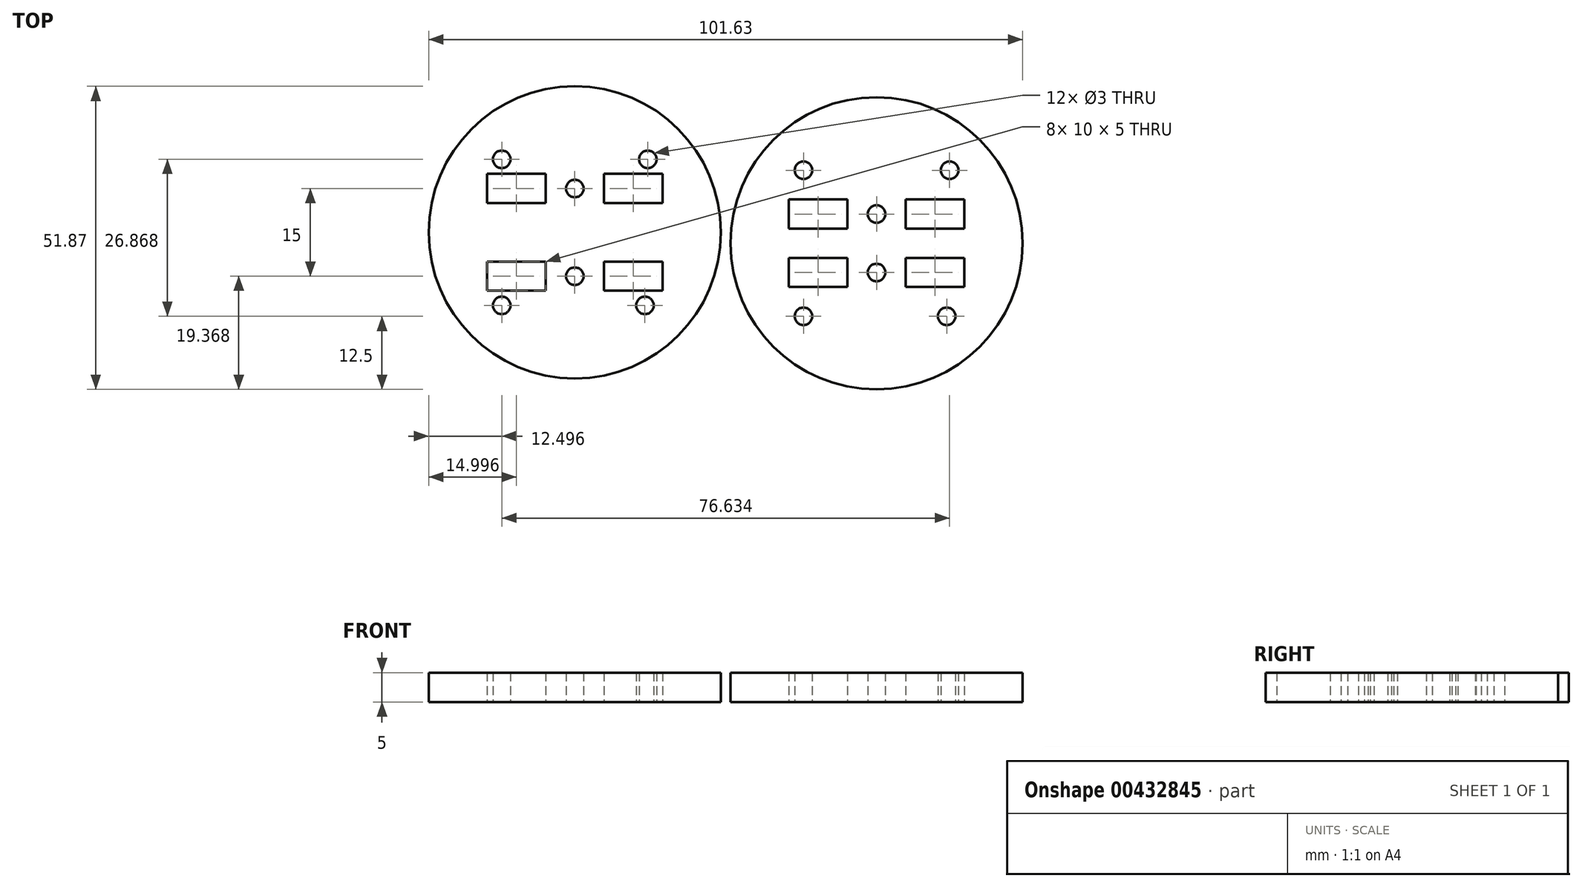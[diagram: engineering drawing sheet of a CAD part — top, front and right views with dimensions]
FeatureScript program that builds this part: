
annotation { "Feature Type Name" : "Feature", "Feature Type Description" : "" }
export const myFeature = defineFeature(function(context is Context, id is Id, definition is map)
    precondition{}
    {
        {
            var Q0;
            Q0=qCreatedBy(makeId("Top.planeOp"),FACE);
            var sketch = newSketch(context, id + "F0", { "sketchPlane" : qUnion([Q0])});
            skCircle(sketch, "E0", {"center": v(0, 0) * mm, "radius": 25 * mm});
            skCircle(sketch, "E1", {"center": v(0, 5) * mm, "radius": 1.5 * mm});
            skCircle(sketch, "E2", {"center": v(0, -5) * mm, "radius": 1.5 * mm});
            skLineSegment(sketch, "E3.bottom", {"start": v(-15, 7.5) * mm, "end": v(-5, 7.5) * mm});
            skLineSegment(sketch, "E3.top", {"start": v(-15, 2.5) * mm, "end": v(-5, 2.5) * mm});
            skLineSegment(sketch, "E3.left", {"start": v(-15, 7.5) * mm, "end": v(-15, 2.5) * mm});
            skLineSegment(sketch, "E3.right", {"start": v(-5, 7.5) * mm, "end": v(-5, 2.5) * mm});
            skLineSegment(sketch, "E4.bottom", {"start": v(5, 7.5) * mm, "end": v(15, 7.5) * mm});
            skLineSegment(sketch, "E4.top", {"start": v(5, 2.5) * mm, "end": v(15, 2.5) * mm});
            skLineSegment(sketch, "E4.left", {"start": v(5, 7.5) * mm, "end": v(5, 2.5) * mm});
            skLineSegment(sketch, "E4.right", {"start": v(15, 7.5) * mm, "end": v(15, 2.5) * mm});
            skLineSegment(sketch, "E5.bottom", {"start": v(-15, -2.5) * mm, "end": v(-5, -2.5) * mm});
            skLineSegment(sketch, "E5.top", {"start": v(-15, -7.5) * mm, "end": v(-5, -7.5) * mm});
            skLineSegment(sketch, "E5.left", {"start": v(-15, -2.5) * mm, "end": v(-15, -7.5) * mm});
            skLineSegment(sketch, "E5.right", {"start": v(-5, -2.5) * mm, "end": v(-5, -7.5) * mm});
            skLineSegment(sketch, "E6.bottom", {"start": v(5, -2.5) * mm, "end": v(15, -2.5) * mm});
            skLineSegment(sketch, "E6.top", {"start": v(5, -7.5) * mm, "end": v(15, -7.5) * mm});
            skLineSegment(sketch, "E6.left", {"start": v(5, -2.5) * mm, "end": v(5, -7.5) * mm});
            skLineSegment(sketch, "E6.right", {"start": v(15, -2.5) * mm, "end": v(15, -7.5) * mm});
            skCircle(sketch, "E7", {"center": v(-12.5, 12.5) * mm, "radius": 1.5 * mm});
            skCircle(sketch, "E8", {"center": v(12.5, 12.5) * mm, "radius": 1.5 * mm});
            skCircle(sketch, "E9", {"center": v(12, -12.5) * mm, "radius": 1.5 * mm});
            skCircle(sketch, "E10", {"center": v(-12.5, -12.5) * mm, "radius": 1.5 * mm});
            skSolve(sketch);
        }
        {
            var Q0;
            Q0=makeQuery(id+"F0.imprint","IMPRINT",FACE,{"disambiguationData":[TD([[makeQuery(id+"F0.imprint","IMPRINT",EDGE,{"derivedFrom":sQuery(id+"F0.wireOp",EDGE,"E0")}),1.0]])]});
            extrude(context, id + "F1", {"entities" : qUnion([Q0]), "depth" : 5 * mm});
        }
        {
            var Q0;
            Q0=qCreatedBy(makeId("Top.planeOp"),FACE);
            var sketch = newSketch(context, id + "F2", { "sketchPlane" : qUnion([Q0])});
            skCircle(sketch, "E11", {"center": v(-51.63, 1.87) * mm, "radius": 25 * mm});
            skCircle(sketch, "E12", {"center": v(-51.63, 9.37) * mm, "radius": 1.5 * mm});
            skCircle(sketch, "E13", {"center": v(-51.63, -5.63) * mm, "radius": 1.5 * mm});
            skLineSegment(sketch, "E14.bottom", {"start": v(-66.63, 11.87) * mm, "end": v(-56.63, 11.87) * mm});
            skLineSegment(sketch, "E14.top", {"start": v(-66.63, 6.87) * mm, "end": v(-56.63, 6.87) * mm});
            skLineSegment(sketch, "E14.left", {"start": v(-66.63, 11.87) * mm, "end": v(-66.63, 6.87) * mm});
            skLineSegment(sketch, "E14.right", {"start": v(-56.63, 11.87) * mm, "end": v(-56.63, 6.87) * mm});
            skLineSegment(sketch, "E15.bottom", {"start": v(-46.63, 11.87) * mm, "end": v(-36.63, 11.87) * mm});
            skLineSegment(sketch, "E15.top", {"start": v(-46.63, 6.87) * mm, "end": v(-36.63, 6.87) * mm});
            skLineSegment(sketch, "E15.left", {"start": v(-46.63, 11.87) * mm, "end": v(-46.63, 6.87) * mm});
            skLineSegment(sketch, "E15.right", {"start": v(-36.63, 11.87) * mm, "end": v(-36.63, 6.87) * mm});
            skLineSegment(sketch, "E16.bottom", {"start": v(-66.63, -3.13) * mm, "end": v(-56.63, -3.13) * mm});
            skLineSegment(sketch, "E16.top", {"start": v(-66.63, -8.13) * mm, "end": v(-56.63, -8.13) * mm});
            skLineSegment(sketch, "E16.left", {"start": v(-66.63, -3.13) * mm, "end": v(-66.63, -8.13) * mm});
            skLineSegment(sketch, "E16.right", {"start": v(-56.63, -3.13) * mm, "end": v(-56.63, -8.13) * mm});
            skLineSegment(sketch, "E17.bottom", {"start": v(-46.63, -3.13) * mm, "end": v(-36.63, -3.13) * mm});
            skLineSegment(sketch, "E17.top", {"start": v(-46.63, -8.13) * mm, "end": v(-36.63, -8.13) * mm});
            skLineSegment(sketch, "E17.left", {"start": v(-46.63, -3.13) * mm, "end": v(-46.63, -8.13) * mm});
            skLineSegment(sketch, "E17.right", {"start": v(-36.63, -3.13) * mm, "end": v(-36.63, -8.13) * mm});
            skCircle(sketch, "E18", {"center": v(-64.13, 14.37) * mm, "radius": 1.5 * mm});
            skCircle(sketch, "E19", {"center": v(-39.13, 14.37) * mm, "radius": 1.5 * mm});
            skCircle(sketch, "E20", {"center": v(-39.63, -10.63) * mm, "radius": 1.5 * mm});
            skCircle(sketch, "E21", {"center": v(-64.13, -10.63) * mm, "radius": 1.5 * mm});
            skSolve(sketch);
        }
        {
            var Q0;
            Q0=makeQuery(id+"F2.imprint","IMPRINT",FACE,{"disambiguationData":[TD([[makeQuery(id+"F2.imprint","IMPRINT",EDGE,{"derivedFrom":sQuery(id+"F2.wireOp",EDGE,"E11")}),1.0]])]});
            extrude(context, id + "F3", {"entities" : qUnion([Q0]), "depth" : 5 * mm});
        }
    });
